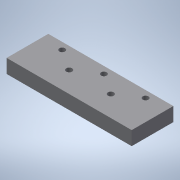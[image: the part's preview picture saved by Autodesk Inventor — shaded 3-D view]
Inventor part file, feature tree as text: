
AUTODESK INVENTOR PART (.ipt)
format: ipt  version: 2021 (Build 250183000, 183)  size: 147,456 bytes
history: native  units: in
note: dims shown in document units (in); Inventor stores cm internally (conversion verified against a paired STEP export)
features: extrude x5, sketch x5
ambient origin geometry x8: Origin, YZ Plane, XZ Plane, XY Plane, X Axis, Y Axis, Z Axis, Center Point
bodies: Solid1 (feature_tree)
feature tree (10):
  extrude  "Extrusion1"  Depth=1.1811in
  extrude  "Extrusion2"  Depth=0.3937in
  extrude  "Extrusion4"  Depth=0.1614in
  extrude  "Extrusion5"  Depth=0.1969in
  extrude  "Extrusion6"  Depth=0.1772in
  sketch  "Sketch1"  dims[d0=3.5433in d5=1.1811in]
  sketch  "Sketch2"  dims[d6=0.3937in d7=0.0in d8=0.1614in]
  sketch  "Sketch4"  dims[d10=0.1614in d11=0.1614in]
  sketch  "Sketch5"  dims[d12=0.1969in d13=0.1969in]
  sketch  "Sketch6"  dims[d14=0.1969in d15=0.5906in d16=1.1811in d17=1.1811in d18=0.3937in d19=0.0in d26=0.2756in d28=0.2756in d29=0.2756in d30=0.1772in d31=0.0in d32=0.1654in d34=0.1654in d35=1.1811in d36=1.1811in d37=0.5906in d38=0.5906in d39=0.3937in d40=0.0in d41=0.2756in d43=0.2756in d44=0.1772in d45=0.0in]
